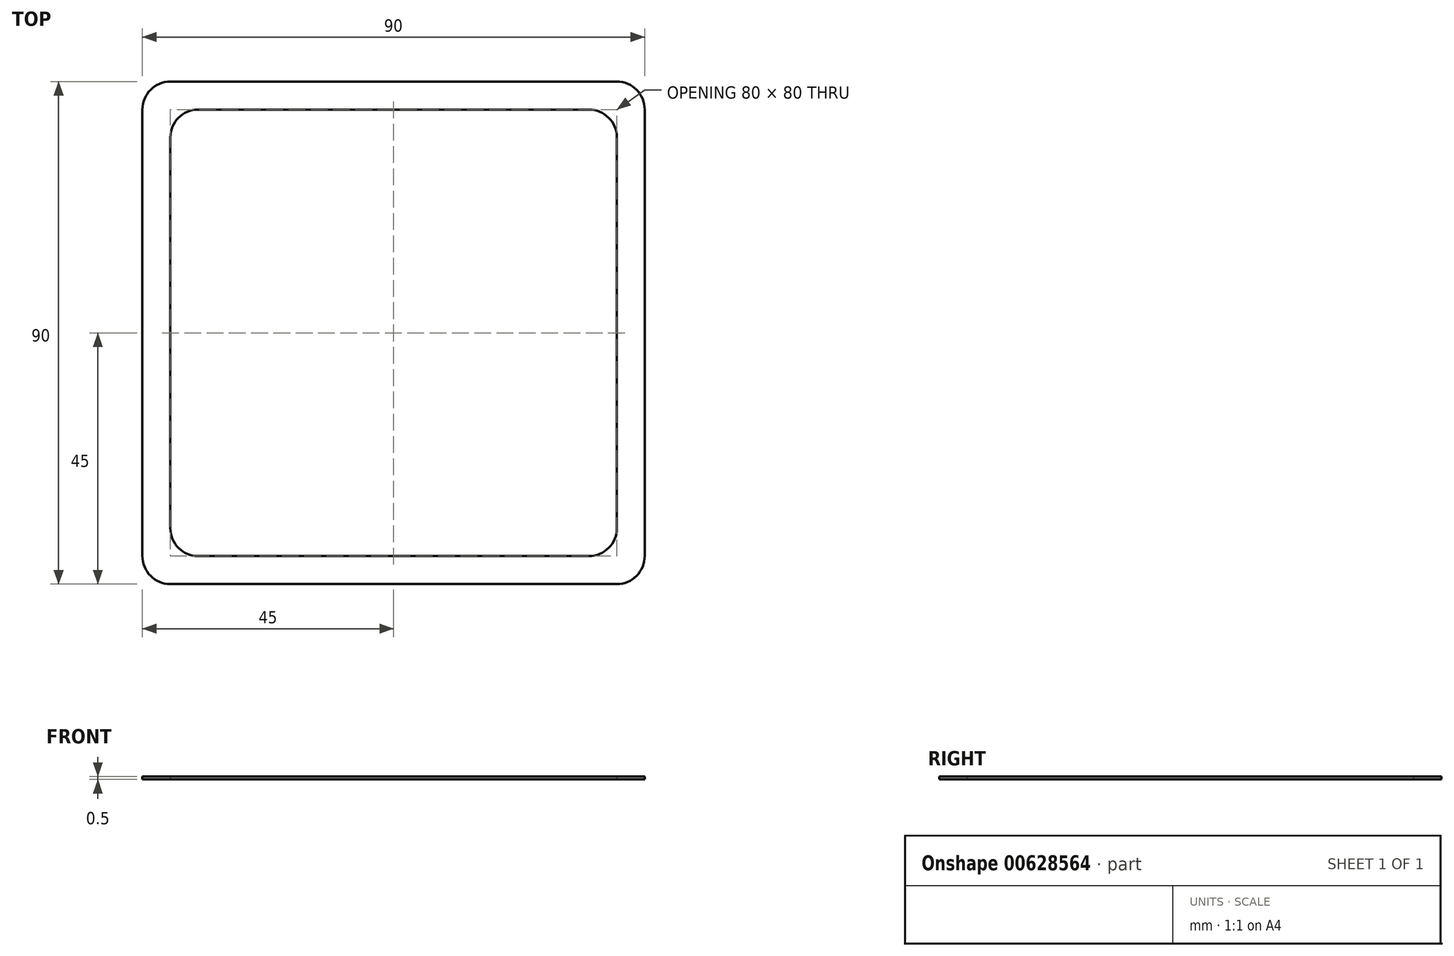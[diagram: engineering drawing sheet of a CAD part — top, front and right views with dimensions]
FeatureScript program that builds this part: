
annotation { "Feature Type Name" : "Feature", "Feature Type Description" : "" }
export const myFeature = defineFeature(function(context is Context, id is Id, definition is map)
    precondition{}
    {
        {
            var Q0;
            Q0=qCreatedBy(makeId("Top.planeOp"),FACE);
            var sketch = newSketch(context, id + "F0", { "sketchPlane" : qUnion([Q0])});
            skLineSegment(sketch, "E0.bottom", {"start": v(-40, 45) * mm, "end": v(40, 45) * mm});
            skLineSegment(sketch, "E0.top", {"start": v(-40, -45) * mm, "end": v(40, -45) * mm});
            skLineSegment(sketch, "E0.left", {"start": v(-45, 40) * mm, "end": v(-45, -40) * mm});
            skLineSegment(sketch, "E0.right", {"start": v(45, 40) * mm, "end": v(45, -40) * mm});
            skPoint(sketch, "E1", {"position": v(-45, 0) * mm});
            skPoint(sketch, "E2", {"position": v(0, 45) * mm});
            skPoint(sketch, "E3.visualSharp", {"position": v(-45, 45) * mm});
            skArc(sketch, "E3.filletArc", {"start": v(-40, 45) * mm, "mid": v(-43.54, 43.54) * mm, "end": v(-45, 40) * mm});
            skPoint(sketch, "E4.visualSharp", {"position": v(45, 45) * mm});
            skArc(sketch, "E4.filletArc", {"start": v(45, 40) * mm, "mid": v(43.54, 43.54) * mm, "end": v(40, 45) * mm});
            skPoint(sketch, "E5.visualSharp", {"position": v(45, -45) * mm});
            skArc(sketch, "E5.filletArc", {"start": v(40, -45) * mm, "mid": v(43.54, -43.54) * mm, "end": v(45, -40) * mm});
            skPoint(sketch, "E6.visualSharp", {"position": v(-45, -45) * mm});
            skArc(sketch, "E6.filletArc", {"start": v(-45, -40) * mm, "mid": v(-43.54, -43.54) * mm, "end": v(-40, -45) * mm});
            skLineSegment(sketch, "E7.0", {"start": v(-35, 40) * mm, "end": v(35, 40) * mm});
            skLineSegment(sketch, "E7.1", {"start": v(-40, 35) * mm, "end": v(-40, -35) * mm});
            skLineSegment(sketch, "E7.2", {"start": v(-35, -40) * mm, "end": v(35, -40) * mm});
            skLineSegment(sketch, "E7.3", {"start": v(40, 35) * mm, "end": v(40, -35) * mm});
            skArc(sketch, "E8.filletArc", {"start": v(-35, 40) * mm, "mid": v(-38.54, 38.54) * mm, "end": v(-40, 35) * mm});
            skArc(sketch, "E9.filletArc", {"start": v(40, 35) * mm, "mid": v(38.54, 38.54) * mm, "end": v(35, 40) * mm});
            skArc(sketch, "E10.filletArc", {"start": v(35, -40) * mm, "mid": v(38.54, -38.54) * mm, "end": v(40, -35) * mm});
            skArc(sketch, "E11.filletArc", {"start": v(-40, -35) * mm, "mid": v(-38.54, -38.54) * mm, "end": v(-35, -40) * mm});
            skSolve(sketch);
        }
        {
            var Q0;
            Q0=makeQuery(id+"F0.imprint","IMPRINT",FACE,{"disambiguationData":[TD([[makeQuery(id+"F0.imprint","IMPRINT",EDGE,{"derivedFrom":sQuery(id+"F0.wireOp",EDGE,"E0.bottom")}),-1.0]])]});
            extrude(context, id + "F1", {"entities" : qUnion([Q0]), "depth" : .5 * mm, "offsetDistance" : 25 * mm});
        }
    });
